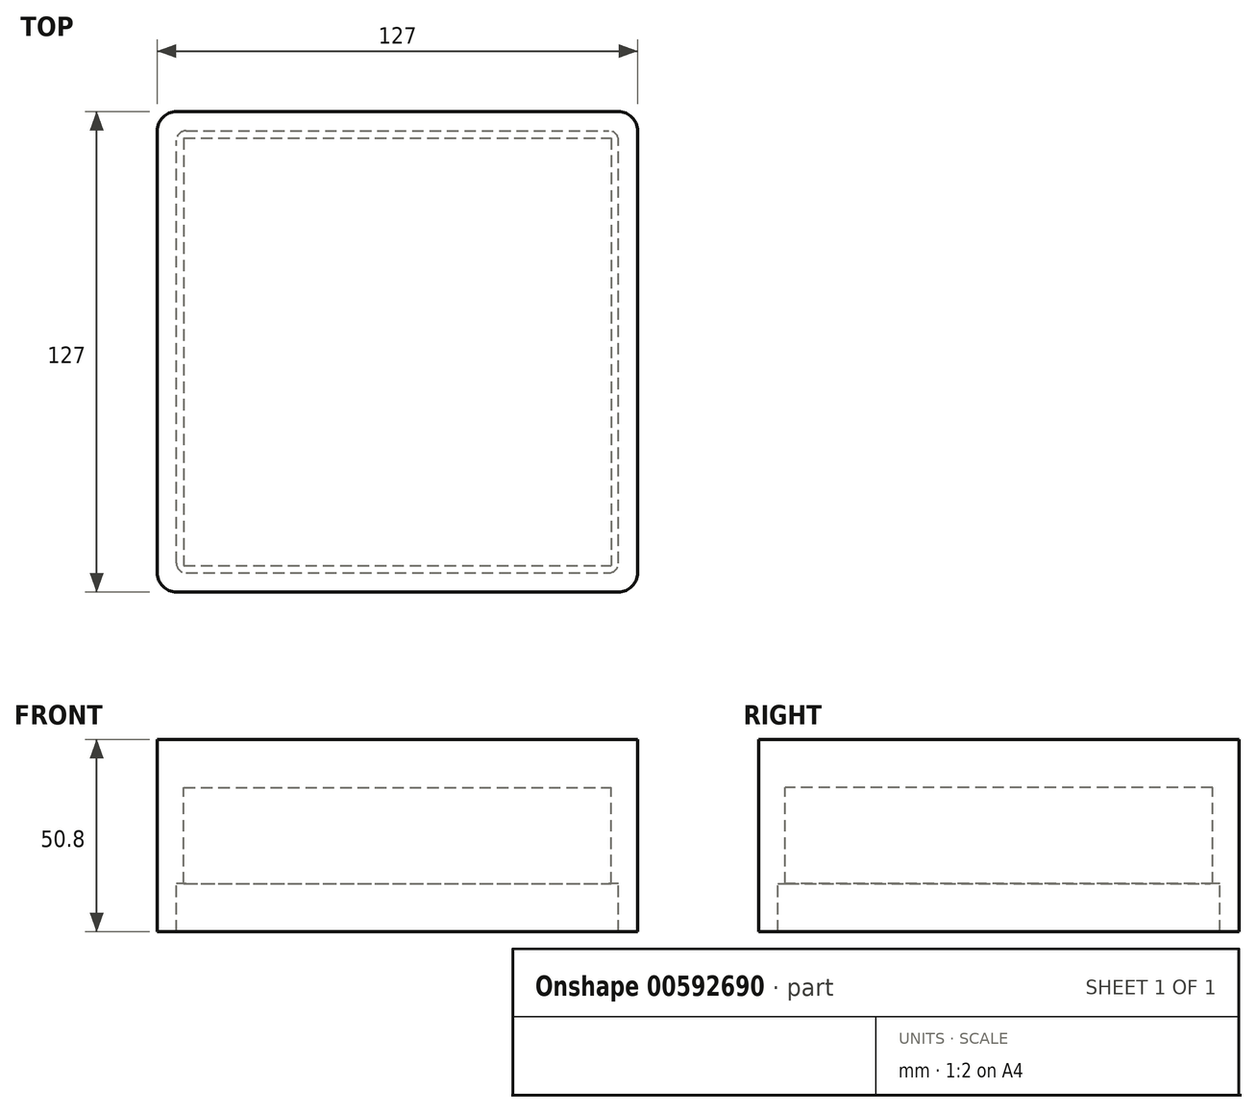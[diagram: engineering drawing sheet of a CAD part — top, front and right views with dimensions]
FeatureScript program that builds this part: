
annotation { "Feature Type Name" : "Feature", "Feature Type Description" : "" }
export const myFeature = defineFeature(function(context is Context, id is Id, definition is map)
    precondition{}
    {
        {
            var Q0;
            Q0=qCreatedBy(makeId("Top.planeOp"),FACE);
            var sketch = newSketch(context, id + "F0", { "sketchPlane" : qUnion([Q0])});
            skLineSegment(sketch, "E0.bottom", {"start": v(-56.52, 56.52) * mm, "end": v(56.52, 56.52) * mm});
            skLineSegment(sketch, "E0.top", {"start": v(-56.52, -56.52) * mm, "end": v(56.52, -56.52) * mm});
            skLineSegment(sketch, "E0.left", {"start": v(-56.52, 56.52) * mm, "end": v(-56.52, -56.52) * mm});
            skLineSegment(sketch, "E0.right", {"start": v(56.52, 56.52) * mm, "end": v(56.52, -56.52) * mm});
            skLineSegment(sketch, "E1.bottom", {"start": v(63.5, -63.5) * mm, "end": v(-63.5, -63.5) * mm});
            skLineSegment(sketch, "E1.top", {"start": v(63.5, 63.5) * mm, "end": v(-63.5, 63.5) * mm});
            skLineSegment(sketch, "E1.left", {"start": v(63.5, -63.5) * mm, "end": v(63.5, 63.5) * mm});
            skLineSegment(sketch, "E1.right", {"start": v(-63.5, -63.5) * mm, "end": v(-63.5, 63.5) * mm});
            skPoint(sketch, "E1.middle", {"position": v(0, 0) * mm});
            skSolve(sketch);
        }
        {
            var Q0;
            Q0=qSketchRegion(id+"F0",true);
            extrude(context, id + "F1", {"entities" : qUnion([Q0]), "oppositeDirection" : true, "depth" : 38.1 * mm, "offsetDistance" : 25.4 * mm});
        }
        {
            var Q0;
            Q0=qCreatedBy(makeId("Top.planeOp"),FACE);
            var sketch = newSketch(context, id + "F2", { "sketchPlane" : qUnion([Q0])});
            skLineSegment(sketch, "E2.bottom", {"start": v(-56.52, 56.52) * mm, "end": v(56.52, 56.52) * mm});
            skLineSegment(sketch, "E2.top", {"start": v(-56.52, -56.52) * mm, "end": v(56.52, -56.52) * mm});
            skLineSegment(sketch, "E2.left", {"start": v(-56.52, 56.52) * mm, "end": v(-56.52, -56.52) * mm});
            skLineSegment(sketch, "E2.right", {"start": v(56.52, 56.52) * mm, "end": v(56.52, -56.52) * mm});
            skPoint(sketch, "E2.middle", {"position": v(0, 0) * mm});
            skSolve(sketch);
        }
        {
            var Q0;
            Q0=makeQuery(id+"F2.imprint","IMPRINT",FACE,{"disambiguationData":[TD([[makeQuery(id+"F2.imprint","IMPRINT",EDGE,{"derivedFrom":sQuery(id+"F2.wireOp",EDGE,"E2.bottom")}),-1.0]])]});
            extrude(context, id + "F3", {"entities" : qUnion([Q0]), "operationType" : NewBodyOperationType.ADD, "oppositeDirection" : true, "depth" : 12.7 * mm, "offsetDistance" : 25.4 * mm});
        }
        {
            var Q0;
            Q0=makeQuery(id+"F1.opExtrude","SWEPT_EDGE",EDGE,{"disambiguationData":[OSD([sQuery(id+"F0.wireOp",EDGE,"E1.bottom"),sQuery(id+"F0.wireOp",EDGE,"E1.right")])]});
            var Q1;
            Q1=makeQuery(id+"F1.opExtrude","SWEPT_EDGE",EDGE,{"disambiguationData":[OSD([sQuery(id+"F0.wireOp",EDGE,"E1.top"),sQuery(id+"F0.wireOp",EDGE,"E1.right")])]});
            var Q2;
            Q2=makeQuery(id+"F1.opExtrude","SWEPT_EDGE",EDGE,{"disambiguationData":[OSD([sQuery(id+"F0.wireOp",EDGE,"E1.top"),sQuery(id+"F0.wireOp",EDGE,"E1.left")])]});
            var Q3;
            Q3=makeQuery(id+"F1.opExtrude","SWEPT_EDGE",EDGE,{"disambiguationData":[OSD([sQuery(id+"F0.wireOp",EDGE,"E1.bottom"),sQuery(id+"F0.wireOp",EDGE,"E1.left")])]});
            fillet(context, id + "F4", {"entities" : qUnion([Q0, Q1, Q2, Q3]), "radius" : 5.08 * mm, "tangentPropagation" : true, "allowEdgeOverflow" : false});
        }
        {
            var Q0;
            Q0=makeQuery(id+"F1.opExtrude","CAP_FACE",FACE,{"disambiguationData":[OSD([sQuery(id+"F0.wireOp",EDGE,"E0.bottom"),sQuery(id+"F0.wireOp",EDGE,"E0.top"),sQuery(id+"F0.wireOp",EDGE,"E0.left"),sQuery(id+"F0.wireOp",EDGE,"E0.right"),sQuery(id+"F0.wireOp",EDGE,"E1.bottom"),sQuery(id+"F0.wireOp",EDGE,"E1.top"),sQuery(id+"F0.wireOp",EDGE,"E1.left"),sQuery(id+"F0.wireOp",EDGE,"E1.right")])],"isStart":false});
            var sketch = newSketch(context, id + "F5", { "sketchPlane" : qUnion([Q0])});
            skLineSegment(sketch, "E3.bottom", {"start": v(-58.42, -58.42) * mm, "end": v(58.42, -58.42) * mm});
            skLineSegment(sketch, "E3.top", {"start": v(-58.42, 58.42) * mm, "end": v(58.42, 58.42) * mm});
            skLineSegment(sketch, "E3.left", {"start": v(-58.42, 58.42) * mm, "end": v(-58.42, -58.42) * mm});
            skLineSegment(sketch, "E3.right", {"start": v(58.42, 58.42) * mm, "end": v(58.42, -58.42) * mm});
            skPoint(sketch, "E3.middle", {"position": v(0, 0) * mm});
            skSolve(sketch);
        }
        {
            var Q0;
            Q0=makeQuery(id+"F5.imprint","IMPRINT",FACE,{"disambiguationData":[TD([[makeQuery(id+"F5.imprint","IMPRINT",EDGE,{"derivedFrom":sQuery(id+"F5.wireOp",EDGE,"E3.bottom")}),-1.0]])]});
            extrude(context, id + "F6", {"entities" : qUnion([Q0]), "operationType" : NewBodyOperationType.ADD, "depth" : 12.7 * mm, "offsetDistance" : 25.4 * mm});
        }
        {
            var Q0;
            Q0=makeQuery(id+"F6.opExtrude","SWEPT_EDGE",EDGE,{"disambiguationData":[OSD([sQuery(id+"F5.wireOp",EDGE,"E3.top"),sQuery(id+"F5.wireOp",EDGE,"E3.left")])]});
            var Q1;
            Q1=makeQuery(id+"F6.opExtrude","SWEPT_EDGE",EDGE,{"disambiguationData":[OSD([sQuery(id+"F5.wireOp",EDGE,"E3.top"),sQuery(id+"F5.wireOp",EDGE,"E3.right")])]});
            var Q2;
            Q2=makeQuery(id+"F6.opExtrude","SWEPT_EDGE",EDGE,{"disambiguationData":[OSD([sQuery(id+"F5.wireOp",EDGE,"E3.bottom"),sQuery(id+"F5.wireOp",EDGE,"E3.right")])]});
            var Q3;
            Q3=makeQuery(id+"F6.opExtrude","SWEPT_EDGE",EDGE,{"disambiguationData":[OSD([sQuery(id+"F5.wireOp",EDGE,"E3.bottom"),sQuery(id+"F5.wireOp",EDGE,"E3.left")])]});
            fillet(context, id + "F7", {"entities" : qUnion([Q0, Q1, Q2, Q3]), "radius" : 2.54 * mm, "tangentPropagation" : true, "allowEdgeOverflow" : false});
        }
    });
